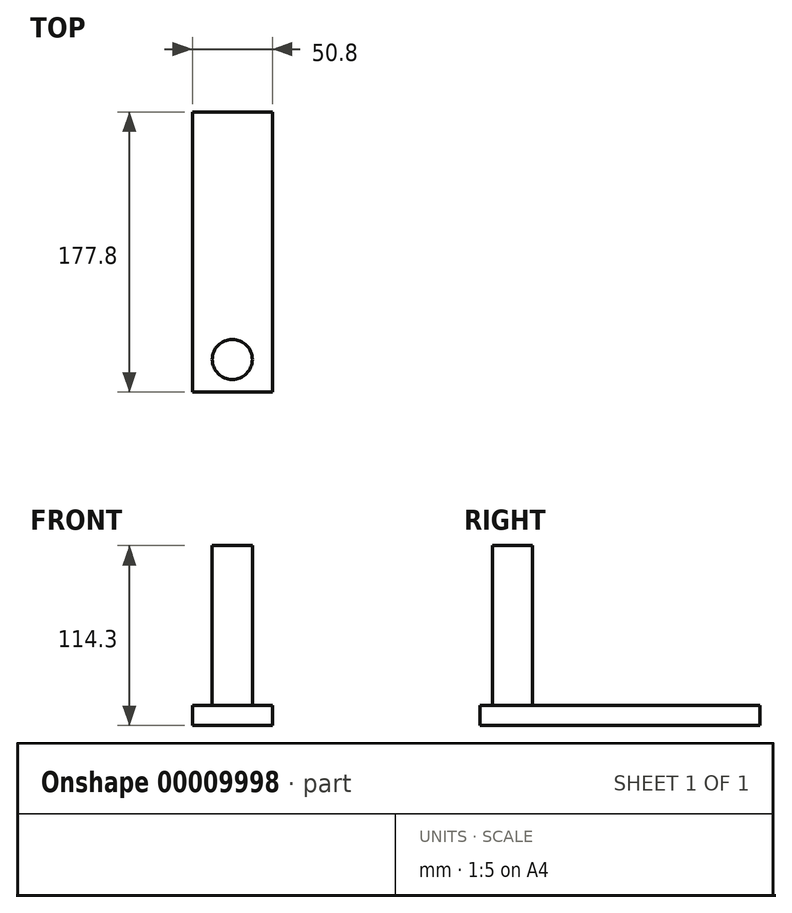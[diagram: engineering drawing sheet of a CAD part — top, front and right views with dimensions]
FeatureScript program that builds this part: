
annotation { "Feature Type Name" : "Feature", "Feature Type Description" : "" }
export const myFeature = defineFeature(function(context is Context, id is Id, definition is map)
    precondition{}
    {
        {
            var Q0;
            Q0=qCreatedBy(makeId("Top.planeOp"),FACE);
            var sketch = newSketch(context, id + "F0", { "sketchPlane" : qUnion([Q0])});
            skLineSegment(sketch, "E0.bottom", {"start": v(-50.8, 77.34) * mm, "end": v(0, 77.34) * mm});
            skLineSegment(sketch, "E0.top", {"start": v(-50.8, -100.46) * mm, "end": v(0, -100.46) * mm});
            skLineSegment(sketch, "E0.left", {"start": v(-50.8, 77.34) * mm, "end": v(-50.8, -100.46) * mm});
            skLineSegment(sketch, "E0.right", {"start": v(0, 77.34) * mm, "end": v(0, -100.46) * mm});
            skSolve(sketch);
        }
        {
            var Q0;
            Q0=makeQuery(id+"F0.imprint","IMPRINT",FACE,{"disambiguationData":[TD([[makeQuery(id+"F0.imprint","IMPRINT",EDGE,{"derivedFrom":sQuery(id+"F0.wireOp",EDGE,"E0.bottom")}),-1.0]])]});
            extrude(context, id + "F1", {"entities" : qUnion([Q0]), "depth" : 12.7 * mm});
        }
        {
            var Q0;
            Q0=makeQuery(id+"F1.opExtrude","CAP_FACE",FACE,{"disambiguationData":[OSD([sQuery(id+"F0.wireOp",EDGE,"E0.bottom"),sQuery(id+"F0.wireOp",EDGE,"E0.top"),sQuery(id+"F0.wireOp",EDGE,"E0.left"),sQuery(id+"F0.wireOp",EDGE,"E0.right")])],"isStart":false});
            var sketch = newSketch(context, id + "F2", { "sketchPlane" : qUnion([Q0])});
            skCircle(sketch, "E1", {"center": v(-25.4, -79.77) * mm, "radius": 12.7 * mm});
            skSolve(sketch);
        }
        {
            var Q0;
            Q0=makeQuery(id+"F2.imprint","IMPRINT",FACE,{"disambiguationData":[TD([[makeQuery(id+"F2.imprint","IMPRINT",EDGE,{"derivedFrom":sQuery(id+"F2.wireOp",EDGE,"E1")}),1.0]])]});
            extrude(context, id + "F3", {"entities" : qUnion([Q0]), "operationType" : NewBodyOperationType.ADD, "depth" : 101.6 * mm});
        }
    });
